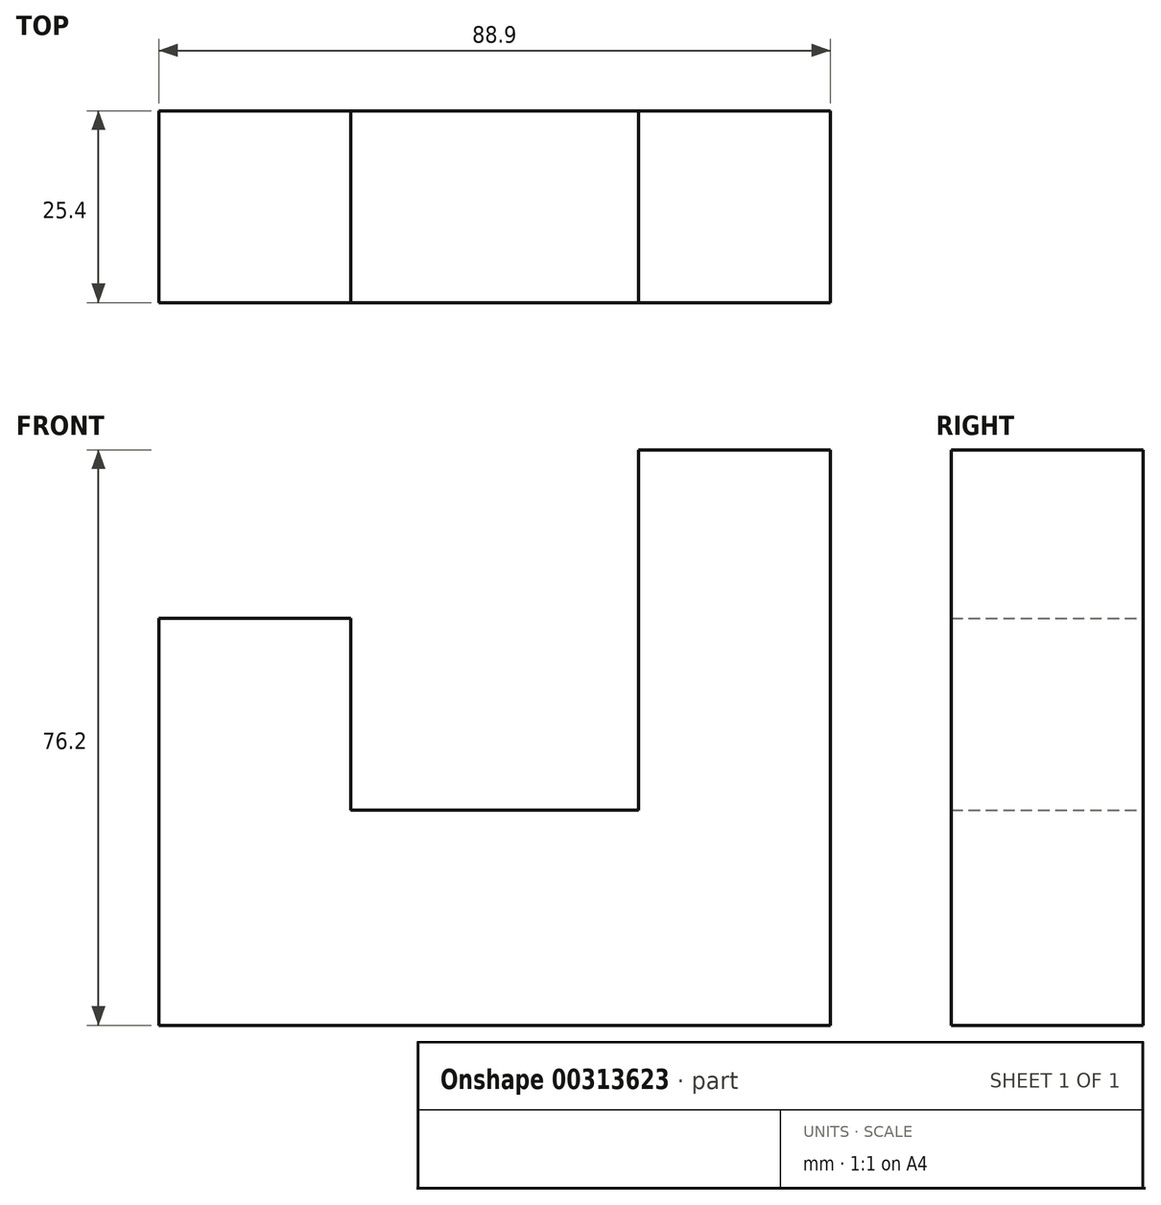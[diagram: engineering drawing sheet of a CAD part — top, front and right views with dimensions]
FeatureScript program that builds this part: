
annotation { "Feature Type Name" : "Feature", "Feature Type Description" : "" }
export const myFeature = defineFeature(function(context is Context, id is Id, definition is map)
    precondition{}
    {
        {
            var Q0;
            Q0=qCreatedBy(makeId("Front.planeOp"),FACE);
            var sketch = newSketch(context, id + "F0", { "sketchPlane" : qUnion([Q0])});
            skLineSegment(sketch, "E0", {"start": v(-31.66, -36.86) * mm, "end": v(57.24, -36.86) * mm});
            skLineSegment(sketch, "E1", {"start": v(57.24, -36.86) * mm, "end": v(57.24, 39.34) * mm});
            skLineSegment(sketch, "E2", {"start": v(57.24, 39.34) * mm, "end": v(31.84, 39.34) * mm});
            skLineSegment(sketch, "E3", {"start": v(31.84, 39.34) * mm, "end": v(31.84, -8.4) * mm});
            skLineSegment(sketch, "E4", {"start": v(31.84, -8.4) * mm, "end": v(-6.26, -8.4) * mm});
            skLineSegment(sketch, "E5", {"start": v(-6.26, -8.4) * mm, "end": v(-6.26, 17) * mm});
            skLineSegment(sketch, "E6", {"start": v(-6.26, 17) * mm, "end": v(-31.66, 17) * mm});
            skLineSegment(sketch, "E7", {"start": v(-31.66, 17) * mm, "end": v(-31.66, -36.86) * mm});
            skSolve(sketch);
        }
        {
            var Q0;
            Q0=makeQuery(id+"F0.imprint","IMPRINT",FACE,{"disambiguationData":[TD([[makeQuery(id+"F0.imprint","IMPRINT",EDGE,{"derivedFrom":sQuery(id+"F0.wireOp",EDGE,"E0")}),1.0]])]});
            extrude(context, id + "F1", {"entities" : qUnion([Q0]), "depth" : 25.4 * mm});
        }
    });
